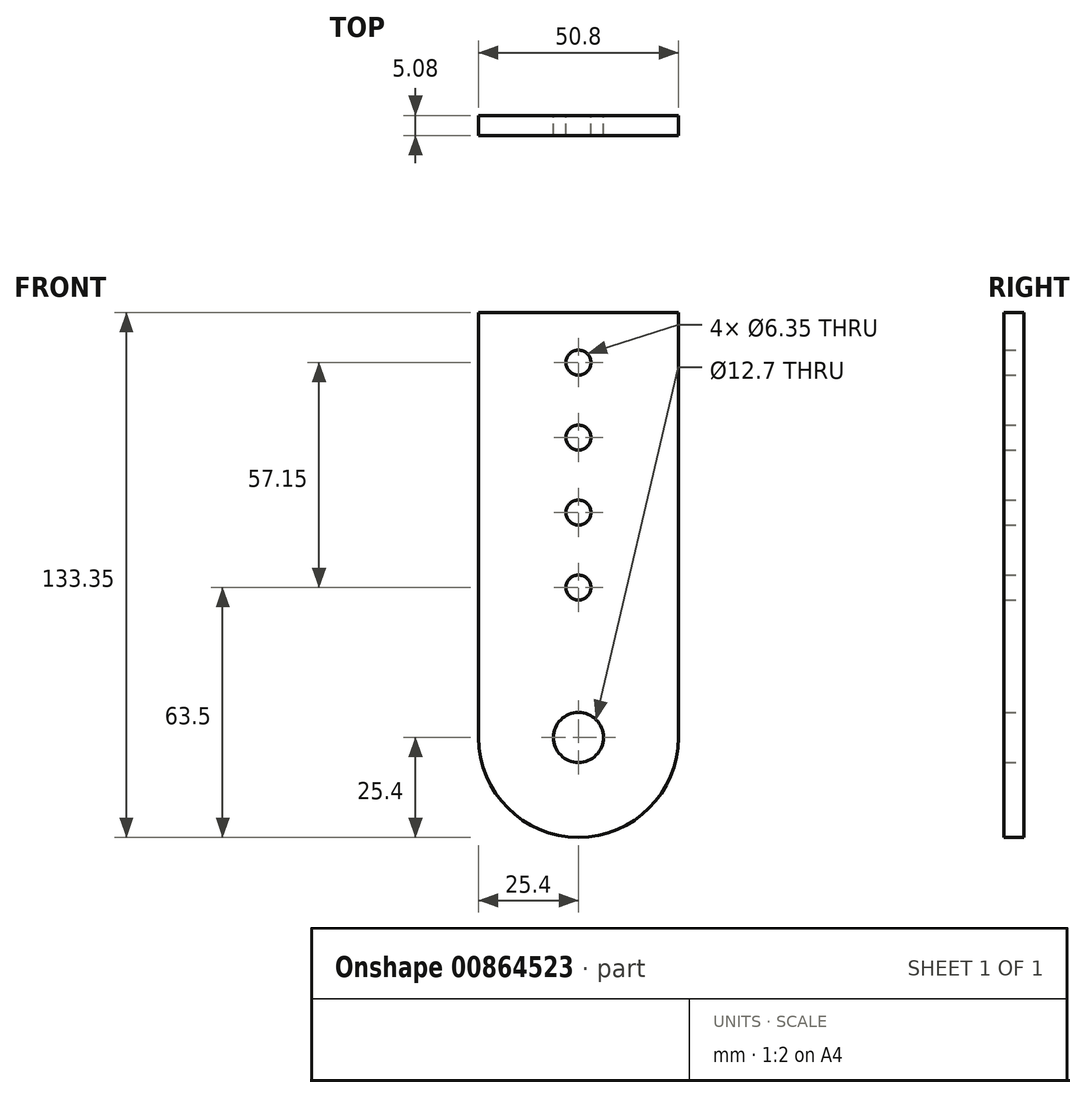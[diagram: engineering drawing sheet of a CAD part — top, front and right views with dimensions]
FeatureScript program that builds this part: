
annotation { "Feature Type Name" : "Feature", "Feature Type Description" : "" }
export const myFeature = defineFeature(function(context is Context, id is Id, definition is map)
    precondition{}
    {
        {
            var Q0;
            Q0=qCreatedBy(makeId("Front.planeOp"),FACE);
            var sketch = newSketch(context, id + "F0", { "sketchPlane" : qUnion([Q0])});
            skCircle(sketch, "E0", {"center": v(0, 0) * mm, "radius": 25.4 * mm});
            skCircle(sketch, "E1", {"center": v(0, 0) * mm, "radius": 6.35 * mm});
            skLineSegment(sketch, "E2.bottom", {"start": v(25.4, 0) * mm, "end": v(-25.4, 0) * mm});
            skLineSegment(sketch, "E3.top", {"start": v(25.4, 107.95) * mm, "end": v(-25.4, 107.95) * mm});
            skLineSegment(sketch, "E3.left", {"start": v(25.4, 0) * mm, "end": v(25.4, 107.95) * mm});
            skLineSegment(sketch, "E3.right", {"start": v(-25.4, 0) * mm, "end": v(-25.4, 107.95) * mm});
            skCircle(sketch, "E4", {"center": v(0, 38.1) * mm, "radius": 3.18 * mm});
            skCircle(sketch, "E5", {"center": v(0, 57.15) * mm, "radius": 3.18 * mm});
            skCircle(sketch, "E6", {"center": v(0, 76.2) * mm, "radius": 3.18 * mm});
            skCircle(sketch, "E7", {"center": v(0, 95.25) * mm, "radius": 3.18 * mm});
            skSolve(sketch);
        }
        {
            var Q0;
            Q0=makeQuery(id+"F0.imprint","IMPRINT",FACE,{"disambiguationData":[TD([[makeQuery(id+"F0.imprint","IMPRINT",EDGE,{"derivedFrom":sQuery(id+"F0.wireOp",EDGE,"E3.top")}),1.0]])]});
            var Q1;
            {var subQ0=sQuery(id+"F0.wireOp",EDGE,"E2.bottom");var subQ4=sQuery(id+"F0.wireOp",EDGE,"E1");var subQ5=makeQuery(id+"F0.imprint","INTERSECT",VERTEX,{"disambiguationData":[OD(0.0)],"derivedFrom":[subQ4,subQ0]});Q1=makeQuery(id+"F0.imprint","IMPRINT",FACE,{"disambiguationData":[TD([[makeQuery(id+"F0.imprint","IMPRINT",EDGE,{"disambiguationData":[TD([[subQ5,-1.0]])],"derivedFrom":subQ4}),-1.0]])]});}
            var Q2;
            {var subQ0=sQuery(id+"F0.wireOp",EDGE,"E2.bottom");var subQ4=sQuery(id+"F0.wireOp",EDGE,"E1");var subQ6=makeQuery(id+"F0.imprint","INTERSECT",VERTEX,{"disambiguationData":[OD(0.0)],"derivedFrom":[subQ4,subQ0]});Q2=makeQuery(id+"F0.imprint","IMPRINT",FACE,{"disambiguationData":[TD([[makeQuery(id+"F0.imprint","IMPRINT",EDGE,{"disambiguationData":[TD([[subQ6,1.0]])],"derivedFrom":subQ4}),-1.0]])]});}
            extrude(context, id + "F1", {"entities" : qUnion([Q0, Q1, Q2]), "endBound" : BoundingType.SYMMETRIC, "depth" : 5.08 * mm, "offsetDistance" : 25.4 * mm});
        }
    });
